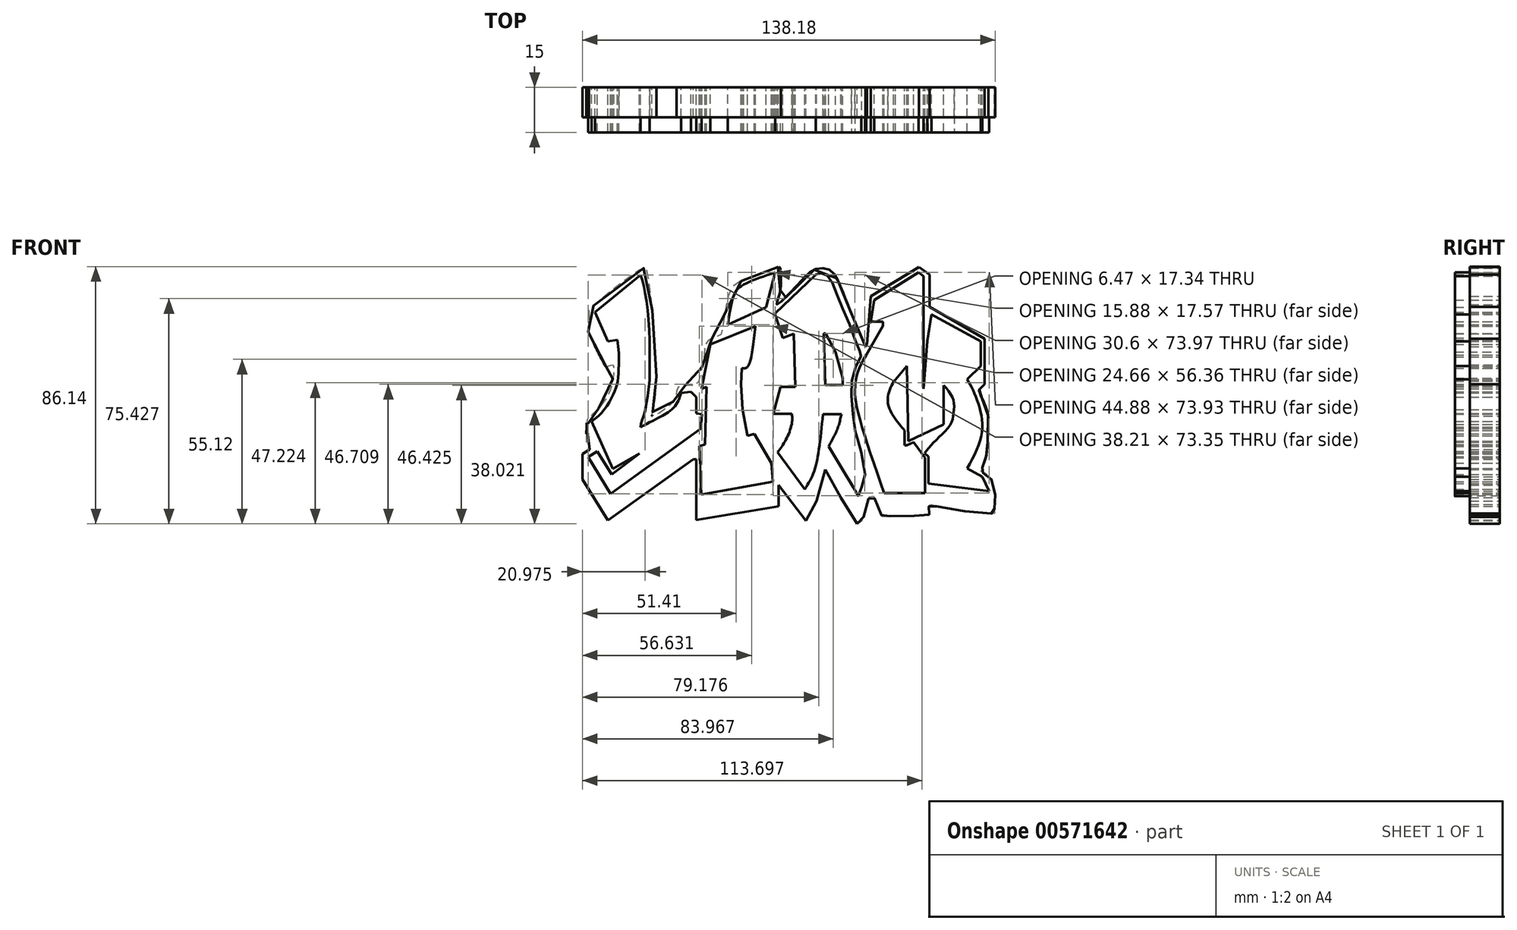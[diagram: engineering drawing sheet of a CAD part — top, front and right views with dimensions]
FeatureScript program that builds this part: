
annotation { "Feature Type Name" : "Feature", "Feature Type Description" : "" }
export const myFeature = defineFeature(function(context is Context, id is Id, definition is map)
    precondition{}
    {
        {
            var Q0;
            Q0=qCreatedBy(makeId("Front.planeOp"),FACE);
            var sketch = newSketch(context, id + "F0", { "sketchPlane" : qUnion([Q0])});
            skLineSegment(sketch, "E0", {"start": v(-63.99, 55.95) * mm, "end": v(-48.71, 68.45) * mm});
            skLineSegment(sketch, "E1", {"start": v(-63.99, 55.95) * mm, "end": v(-59.7, 46.21) * mm});
            skLineSegment(sketch, "E2", {"start": v(-59.7, 46.21) * mm, "end": v(-56.45, 46.65) * mm});
            skFitSpline(sketch, "E3", {"points": [v(-56.45, 46.65) * mm, v(-56.06, 43.07) * mm, v(-56, 38.38) * mm, v(-56.45, 32.7) * mm, v(-57.57, 29.04) * mm, v(-60.63, 23.63) * mm, v(-65.08, 19.34) * mm], "startDerivative": vector(3.26, -24.64) * mm, "endDerivative": vector(-25.33, -21.05) * mm});
            skLineSegment(sketch, "E4", {"start": v(-65.08, 19.34) * mm, "end": v(-58.06, 3.56) * mm});
            skLineSegment(sketch, "E5", {"start": v(-58.06, 3.56) * mm, "end": v(-49.1, 8.6) * mm});
            skLineSegment(sketch, "E6", {"start": v(-49.1, 8.6) * mm, "end": v(-58.36, 1.6) * mm});
            skLineSegment(sketch, "E7", {"start": v(-58.36, 1.6) * mm, "end": v(-63.16, 9.37) * mm});
            skLineSegment(sketch, "E8", {"start": v(-63.16, 9.37) * mm, "end": v(-66.33, 7.42) * mm});
            skLineSegment(sketch, "E9", {"start": v(-66.33, 7.42) * mm, "end": v(-58.72, -4.9) * mm});
            skLineSegment(sketch, "E10", {"start": v(-58.72, -4.9) * mm, "end": v(-28.61, 17) * mm});
            skLineSegment(sketch, "E11", {"start": v(-28.61, 17) * mm, "end": v(-28.12, 21.8) * mm});
            skLineSegment(sketch, "E12", {"start": v(-28.12, 21.8) * mm, "end": v(-30.13, 22) * mm});
            skLineSegment(sketch, "E13", {"start": v(-30.13, 22) * mm, "end": v(-30.13, 27.56) * mm});
            skLineSegment(sketch, "E14", {"start": v(-30.13, 27.56) * mm, "end": v(-31.81, 29.31) * mm});
            skLineSegment(sketch, "E15", {"start": v(-31.81, 29.31) * mm, "end": v(-35.1, 28.96) * mm});
            skFitSpline(sketch, "E16", {"points": [v(-35.1, 28.96) * mm, v(-35.64, 27.42) * mm, v(-36.86, 24.98) * mm, v(-39.26, 22.6) * mm, v(-42.5, 20.74) * mm, v(-48.76, 17.47) * mm], "startDerivative": vector(-3.5, -10.66) * mm, "endDerivative": vector(-23.82, -12.44) * mm});
            skFitSpline(sketch, "E17", {"points": [v(-48.76, 17.47) * mm, v(-48.46, 19.08) * mm, v(-47.3, 22.46) * mm, v(-46.65, 26.08) * mm, v(-45.77, 32) * mm, v(-45.7, 35.08) * mm, v(-45.79, 47.9) * mm, v(-47.16, 62.28) * mm, v(-48.71, 68.45) * mm], "startDerivative": vector(2.53, 21.74) * mm, "endDerivative": vector(-12.5, 41.93) * mm});
            skFitSpline(sketch, "E18", {"points": [v(-19.5, 51.71) * mm, v(-6.66, 57.57) * mm], "startDerivative": vector(12.84, 5.86) * mm, "endDerivative": vector(12.84, 5.86) * mm});
            skFitSpline(sketch, "E19", {"points": [v(-6.66, 57.57) * mm, v(-3.63, 69.28) * mm], "startDerivative": vector(3.03, 11.72) * mm, "endDerivative": vector(3.03, 11.72) * mm});
            skFitSpline(sketch, "E20", {"points": [v(-3.63, 69.28) * mm, v(-14, 65.33) * mm, v(-17.32, 62.09) * mm, v(-19.5, 51.71) * mm], "startDerivative": vector(-31.1, -10.4) * mm, "endDerivative": vector(-4.34, -32.28) * mm});
            skFitSpline(sketch, "E21", {"points": [v(-25.38, 45.16) * mm, v(-10.24, 51.27) * mm], "startDerivative": vector(15.13, 6.11) * mm, "endDerivative": vector(15.13, 6.11) * mm});
            skFitSpline(sketch, "E22", {"points": [v(-10.24, 51.27) * mm, v(-12.86, 37.68) * mm, v(-14.16, 37.15) * mm], "startDerivative": vector(-2.7, -23.89) * mm, "endDerivative": vector(-5.63, -0.3) * mm});
            skFitSpline(sketch, "E23", {"points": [v(-25.38, 45.16) * mm, v(-28.29, 30.32) * mm], "startDerivative": vector(-2.9, -14.84) * mm, "endDerivative": vector(-2.9, -14.84) * mm});
            skFitSpline(sketch, "E24", {"points": [v(-28.29, 30.32) * mm, v(-26.62, 30.97) * mm], "startDerivative": vector(1.66, 0.65) * mm, "endDerivative": vector(1.66, 0.65) * mm});
            skFitSpline(sketch, "E25", {"points": [v(-26.62, 30.97) * mm, v(-27.22, 11.68) * mm], "startDerivative": vector(-0.6, -19.3) * mm, "endDerivative": vector(-0.6, -19.3) * mm});
            skFitSpline(sketch, "E26", {"points": [v(-27.22, 11.68) * mm, v(-29.12, 11.14) * mm], "startDerivative": vector(-1.9, -0.53) * mm, "endDerivative": vector(-1.9, -0.53) * mm});
            skLineSegment(sketch, "E27", {"start": v(-29.12, 11.14) * mm, "end": v(-28.49, -5.09) * mm});
            skLineSegment(sketch, "E28", {"start": v(-28.49, -5.09) * mm, "end": v(-4.46, -0.84) * mm});
            skLineSegment(sketch, "E29", {"start": v(-4.46, -0.84) * mm, "end": v(-4.9, 5.4) * mm});
            skLineSegment(sketch, "E30", {"start": v(-4.9, 5.4) * mm, "end": v(-10.7, 15.23) * mm});
            skLineSegment(sketch, "E31", {"start": v(-10.7, 15.23) * mm, "end": v(-12.9, 14.58) * mm});
            skLineSegment(sketch, "E32", {"start": v(-12.9, 14.58) * mm, "end": v(-14.6, 23.29) * mm});
            skLineSegment(sketch, "E33", {"start": v(-14.6, 23.29) * mm, "end": v(-15.13, 31.9) * mm});
            skLineSegment(sketch, "E34", {"start": v(-15.13, 31.9) * mm, "end": v(-14.9, 37.15) * mm});
            skLineSegment(sketch, "E35", {"start": v(-14.9, 37.15) * mm, "end": v(-14.16, 37.15) * mm});
            skLineSegment(sketch, "E36", {"start": v(-2.91, 9.05) * mm, "end": v(6.26, -3.3) * mm});
            skFitSpline(sketch, "E37", {"points": [v(6.26, -3.3) * mm, v(8.73, 1.14) * mm, v(10.57, 7.5) * mm, v(12.33, 21.75) * mm], "startDerivative": vector(10.14, 16.48) * mm, "endDerivative": vector(3.61, 35.55) * mm});
            skFitSpline(sketch, "E38", {"points": [v(-2.91, 9.05) * mm, v(0, 13.35) * mm, v(1.96, 19.07) * mm, v(1.89, 21.9) * mm], "startDerivative": vector(8.6, 11.07) * mm, "endDerivative": vector(-1.28, 9.71) * mm});
            skFitSpline(sketch, "E39", {"points": [v(1.89, 21.9) * mm, v(-4.33, 21.9) * mm], "startDerivative": vector(-6.21, 0) * mm, "endDerivative": vector(-6.21, 0) * mm});
            skFitSpline(sketch, "E40", {"points": [v(-4.33, 21.9) * mm, v(-1.85, 30.93) * mm], "startDerivative": vector(2.47, 9.03) * mm, "endDerivative": vector(2.47, 9.03) * mm});
            skFitSpline(sketch, "E41", {"points": [v(-1.85, 30.93) * mm, v(3.12, 30.93) * mm], "startDerivative": vector(4.97, 0) * mm, "endDerivative": vector(4.97, 0) * mm});
            skLineSegment(sketch, "E42", {"start": v(3.12, 30.93) * mm, "end": v(2.5, 48.73) * mm});
            skLineSegment(sketch, "E43", {"start": v(2.5, 48.73) * mm, "end": v(-1.1, 47.27) * mm});
            skLineSegment(sketch, "E44", {"start": v(-1.1, 47.27) * mm, "end": v(-3.79, 55.45) * mm});
            skLineSegment(sketch, "E45", {"start": v(-3.79, 55.45) * mm, "end": v(9.91, 68.48) * mm});
            skFitSpline(sketch, "E46", {"points": [v(9.91, 68.48) * mm, v(10.91, 68.88) * mm, v(12.7, 68.93) * mm, v(14.75, 67.08) * mm, v(17.25, 61.24) * mm, v(21.8, 50.32) * mm, v(24.79, 42.68) * mm, v(25.22, 41.9) * mm, v(22.92, 36.66) * mm, v(21.88, 27.23) * mm, v(23.54, 14.44) * mm, v(24.75, 10.56) * mm, v(26.4, 2.38) * mm, v(26.4, 1.28) * mm, v(24.25, -5.6) * mm, v(23.9, -5.25) * mm, v(14.22, 11.02) * mm], "startDerivative": vector(31.9, 15.16) * mm, "endDerivative": vector(-109.87, 180.97) * mm});
            skFitSpline(sketch, "E47", {"points": [v(14.22, 11.02) * mm, v(17.16, 16.81) * mm, v(18.5, 21.85) * mm], "startDerivative": vector(6.3, 11.06) * mm, "endDerivative": vector(2.2, 10.59) * mm});
            skFitSpline(sketch, "E48", {"points": [v(18.5, 21.85) * mm, v(12.33, 21.75) * mm], "startDerivative": vector(-6.18, -0.1) * mm, "endDerivative": vector(-6.18, -0.1) * mm});
            skLineSegment(sketch, "E49", {"start": v(32.81, -4.67) * mm, "end": v(46.5, -4.67) * mm});
            skLineSegment(sketch, "E50", {"start": v(46.5, -4.67) * mm, "end": v(46.5, 7.25) * mm});
            skLineSegment(sketch, "E51", {"start": v(46.5, 7.25) * mm, "end": v(42.63, 12.45) * mm});
            skLineSegment(sketch, "E52", {"start": v(42.63, 12.45) * mm, "end": v(40.38, 11.34) * mm});
            skLineSegment(sketch, "E53", {"start": v(40.38, 11.34) * mm, "end": v(39.69, 11.34) * mm});
            skLineSegment(sketch, "E54", {"start": v(39.69, 11.34) * mm, "end": v(39.69, 16.33) * mm});
            skFitSpline(sketch, "E55", {"points": [v(32.81, -4.67) * mm, v(23.71, 23.9) * mm, v(23.06, 30.37) * mm, v(23.8, 35.37) * mm, v(26.4, 41) * mm], "startDerivative": vector(-27.1, 78.42) * mm, "endDerivative": vector(15.63, 28.91) * mm});
            skFitSpline(sketch, "E56", {"points": [v(39.69, 16.33) * mm, v(37.26, 19.22) * mm, v(34.36, 24.27) * mm, v(34.3, 28.72) * mm, v(36.02, 32.82) * mm], "startDerivative": vector(-10.21, 11.55) * mm, "endDerivative": vector(8.26, 16.36) * mm});
            skLineSegment(sketch, "E57", {"start": v(36.61, 33.4) * mm, "end": v(40.42, 37.94) * mm});
            skLineSegment(sketch, "E58", {"start": v(40.42, 37.94) * mm, "end": v(40.94, 12.76) * mm});
            skLineSegment(sketch, "E59", {"start": v(40.94, 12.76) * mm, "end": v(52.75, 18.33) * mm});
            skLineSegment(sketch, "E60", {"start": v(52.75, 18.33) * mm, "end": v(52.75, 31.45) * mm});
            skLineSegment(sketch, "E61", {"start": v(26.88, 41.6) * mm, "end": v(32.39, 51.34) * mm});
            skLineSegment(sketch, "E62", {"start": v(32.39, 51.34) * mm, "end": v(32.39, 52.8) * mm});
            skLineSegment(sketch, "E63", {"start": v(32.39, 52.8) * mm, "end": v(28.32, 52.8) * mm});
            skLineSegment(sketch, "E64", {"start": v(28.32, 52.8) * mm, "end": v(29.45, 60.01) * mm});
            skLineSegment(sketch, "E65", {"start": v(29.45, 60.01) * mm, "end": v(44.4, 69.26) * mm});
            skLineSegment(sketch, "E66", {"start": v(44.4, 69.26) * mm, "end": v(46, 68.08) * mm});
            skLineSegment(sketch, "E67", {"start": v(46, 68.08) * mm, "end": v(46, 30.27) * mm});
            skLineSegment(sketch, "E68", {"start": v(46, 30.27) * mm, "end": v(47.25, 46.36) * mm});
            skLineSegment(sketch, "E69", {"start": v(47.25, 46.36) * mm, "end": v(48.67, 55.2) * mm});
            skLineSegment(sketch, "E70", {"start": v(48.67, 55.2) * mm, "end": v(65.17, 46.12) * mm});
            skLineSegment(sketch, "E71", {"start": v(65.17, 46.12) * mm, "end": v(65.17, 37.93) * mm});
            skLineSegment(sketch, "E72", {"start": v(65.17, 37.93) * mm, "end": v(60.66, 33.48) * mm});
            skFitSpline(sketch, "E73", {"points": [v(60.66, 33.48) * mm, v(62.79, 29.33) * mm, v(65.08, 22.74) * mm, v(65.38, 14.56) * mm, v(60.66, 3.58) * mm], "startDerivative": vector(10.98, -20.03) * mm, "endDerivative": vector(-19.3, -36.15) * mm});
            skFitSpline(sketch, "E74", {"points": [v(60.66, 3.58) * mm, v(65.68, 0.88) * mm], "startDerivative": vector(5.02, -2.7) * mm, "endDerivative": vector(5.02, -2.7) * mm});
            skFitSpline(sketch, "E75", {"points": [v(65.68, 0.88) * mm, v(67.94, -3.97) * mm], "startDerivative": vector(2.26, -4.85) * mm, "endDerivative": vector(2.26, -4.85) * mm});
            skLineSegment(sketch, "E76", {"start": v(67.94, -3.97) * mm, "end": v(47.63, -1.45) * mm});
            skLineSegment(sketch, "E77", {"start": v(47.63, -1.45) * mm, "end": v(47.63, 7.53) * mm});
            skLineSegment(sketch, "E78", {"start": v(47.63, 7.53) * mm, "end": v(46.37, 8.7) * mm});
            skFitSpline(sketch, "E79", {"points": [v(46.37, 8.7) * mm, v(49.9, 12.81) * mm, v(54.76, 17.93) * mm, v(56.1, 22.3) * mm, v(55.85, 26.91) * mm, v(52.75, 31.45) * mm], "startDerivative": vector(15.72, 20.12) * mm, "endDerivative": vector(-18.9, 21.72) * mm});
            skLineSegment(sketch, "E80", {"start": v(26.4, 41) * mm, "end": v(26.88, 41.6) * mm});
            skLineSegment(sketch, "E81", {"start": v(36.02, 32.82) * mm, "end": v(36.61, 33.4) * mm});
            skLineSegment(sketch, "E82", {"start": v(-65.72, 9.95) * mm, "end": v(-68.2, 8.41) * mm});
            skLineSegment(sketch, "E83", {"start": v(-68.2, 8.41) * mm, "end": v(-68.2, 0) * mm});
            skLineSegment(sketch, "E84", {"start": v(-68.2, 0) * mm, "end": v(-59.67, -13.8) * mm});
            skLineSegment(sketch, "E85", {"start": v(-59.67, -13.8) * mm, "end": v(-31.06, 6.64) * mm});
            skLineSegment(sketch, "E86", {"start": v(-31.06, 6.64) * mm, "end": v(-30.07, 6.64) * mm});
            skLineSegment(sketch, "E87", {"start": v(-30.07, 6.64) * mm, "end": v(-30.07, -13.69) * mm});
            skLineSegment(sketch, "E88", {"start": v(-30.07, -13.69) * mm, "end": v(-2.48, -9.1) * mm});
            skLineSegment(sketch, "E89", {"start": v(-2.48, -9.1) * mm, "end": v(-2.48, -1.9) * mm});
            skLineSegment(sketch, "E90", {"start": v(-2.48, -1.9) * mm, "end": v(6.57, -13.91) * mm});
            skLineSegment(sketch, "E91", {"start": v(6.57, -13.91) * mm, "end": v(10.13, -7.26) * mm});
            skLineSegment(sketch, "E92", {"start": v(10.13, -7.26) * mm, "end": v(13.1, 3.3) * mm});
            skLineSegment(sketch, "E93", {"start": v(13.1, 3.3) * mm, "end": v(18.26, -6.08) * mm});
            skLineSegment(sketch, "E94", {"start": v(18.26, -6.08) * mm, "end": v(23.74, -14.93) * mm});
            skPoint(sketch, "E95.10.internal.snap0", {"position": v(8.35, -10.59) * mm});
            skFitSpline(sketch, "E95", {"points": [v(23.74, -14.93) * mm, v(25.9, -12.8) * mm, v(28.62, -5.03) * mm, v(32, -12.32) * mm, v(33.35, -12.48) * mm, v(47.7, -11.98) * mm, v(47.7, -11.3) * mm, v(47.95, -8.62) * mm, v(48.96, -8.7) * mm, v(69.78, -11.4) * mm, v(69.86, -10.59) * mm, v(69.94, -4.68) * mm, v(67.34, 1.62) * mm, v(65.33, 2.38) * mm, v(65.83, 4.39) * mm, v(67.26, 9.5) * mm, v(67.5, 16.98) * mm, v(67.43, 22.43) * mm, v(64.57, 29.73) * mm, v(64.82, 30.24) * mm, v(66.5, 31.83) * mm], "startDerivative": vector(55.31, 23.52) * mm, "endDerivative": vector(54.2, 52.6) * mm});
            skFitSpline(sketch, "E96", {"points": [v(66.5, 31.83) * mm, v(66.5, 47.13) * mm], "startDerivative": vector(0, 15.3) * mm, "endDerivative": vector(0, 15.3) * mm});
            skFitSpline(sketch, "E97", {"points": [v(66.5, 47.13) * mm, v(47.98, 57.7) * mm], "startDerivative": vector(-18.52, 10.58) * mm, "endDerivative": vector(-18.52, 10.58) * mm});
            skFitSpline(sketch, "E98", {"points": [v(47.98, 57.7) * mm, v(47.98, 68.56) * mm], "startDerivative": vector(0, 10.86) * mm, "endDerivative": vector(0, 10.86) * mm});
            skFitSpline(sketch, "E99", {"points": [v(47.98, 68.56) * mm, v(44.52, 71.12) * mm], "startDerivative": vector(-3.46, 2.55) * mm, "endDerivative": vector(-3.46, 2.55) * mm});
            skFitSpline(sketch, "E100", {"points": [v(44.52, 71.12) * mm, v(28.32, 61.24) * mm], "startDerivative": vector(-16.2, -9.87) * mm, "endDerivative": vector(-16.2, -9.87) * mm});
            skFitSpline(sketch, "E101", {"points": [v(28.32, 61.24) * mm, v(27.07, 45.12) * mm], "startDerivative": vector(-1.25, -16.12) * mm, "endDerivative": vector(-1.25, -16.12) * mm});
            skFitSpline(sketch, "E102", {"points": [v(27.07, 45.12) * mm, v(26.4, 44.05) * mm], "startDerivative": vector(-0.68, -1.07) * mm, "endDerivative": vector(-0.68, -1.07) * mm});
            skFitSpline(sketch, "E103", {"points": [v(26.62, 44.4) * mm, v(20.54, 58.71) * mm, v(19.3, 61.98) * mm, v(17.25, 66.78) * mm, v(14.34, 70.25) * mm, v(9.5, 70.25) * mm, v(4.3, 65.71) * mm, v(-3.08, 58.53) * mm, v(-2.42, 61.24) * mm, v(-1.71, 67.52) * mm, v(-2.24, 71.12) * mm, v(-4.08, 70.54) * mm, v(-15.12, 66.39) * mm, v(-19.28, 61.76) * mm, v(-21.71, 48.64) * mm, v(-22.31, 48.14) * mm, v(-26.55, 46.12) * mm, v(-27.2, 43.55) * mm, v(-29.72, 31.83) * mm, v(-30.73, 31.42) * mm, v(-36.31, 30.75) * mm, v(-36.7, 29.2) * mm, v(-38.03, 25.71) * mm, v(-44.79, 21.22) * mm, v(-44.75, 22.4) * mm, v(-43.78, 27.56) * mm, v(-43.78, 44.4) * mm, v(-46.58, 69.86) * mm, v(-47.83, 70.7) * mm, v(-65.8, 56.99) * mm, v(-66, 56.44) * mm, v(-66.25, 49.55) * mm, v(-65.95, 48.8) * mm, v(-60.2, 37.57) * mm, v(-59.7, 37.72) * mm, v(-58.11, 38.22) * mm, v(-58.3, 32.07) * mm, v(-60.64, 26.54) * mm, v(-65.08, 21.5) * mm, v(-66.51, 20.24) * mm, v(-66.8, 17.22) * mm, v(-66.8, 12.35) * mm, v(-65.72, 9.95) * mm], "startDerivative": vector(-178.63, 414.35) * mm, "endDerivative": vector(79.74, -124.12) * mm});
            skLineSegment(sketch, "E104", {"start": v(-14.16, 37.15) * mm, "end": v(-14.16, 37.15) * mm});
            skLineSegment(sketch, "E105", {"start": v(12.53, 48.86) * mm, "end": v(13.18, 48.86) * mm});
            skLineSegment(sketch, "E106", {"start": v(13.18, 48.86) * mm, "end": v(16.5, 42.6) * mm});
            skLineSegment(sketch, "E107", {"start": v(16.5, 42.6) * mm, "end": v(19, 33.87) * mm});
            skLineSegment(sketch, "E108", {"start": v(19, 33.87) * mm, "end": v(19, 31.52) * mm});
            skLineSegment(sketch, "E109", {"start": v(19, 31.52) * mm, "end": v(13.06, 31.52) * mm});
            skLineSegment(sketch, "E110", {"start": v(13.06, 31.52) * mm, "end": v(12.53, 48.86) * mm});
            skSolve(sketch);
        }
        {
            var Q0;
            Q0=makeQuery(id+"F0.imprint","IMPRINT",FACE,{"disambiguationData":[TD([[makeQuery(id+"F0.imprint","IMPRINT",EDGE,{"derivedFrom":sQuery(id+"F0.wireOp",EDGE,"E0")}),-1.0]])]});
            var Q1;
            Q1=makeQuery(id+"F0.imprint","IMPRINT",FACE,{"disambiguationData":[TD([[makeQuery(id+"F0.imprint","IMPRINT",EDGE,{"derivedFrom":sQuery(id+"F0.wireOp",EDGE,"E21")}),-1.0]])]});
            var Q2;
            Q2=makeQuery(id+"F0.imprint","IMPRINT",FACE,{"disambiguationData":[TD([[makeQuery(id+"F0.imprint","IMPRINT",EDGE,{"derivedFrom":sQuery(id+"F0.wireOp",EDGE,"E18")}),1.0]])]});
            var Q3;
            Q3=makeQuery(id+"F0.imprint","IMPRINT",FACE,{"disambiguationData":[TD([[makeQuery(id+"F0.imprint","IMPRINT",EDGE,{"derivedFrom":sQuery(id+"F0.wireOp",EDGE,"E36")}),1.0]])]});
            var Q4;
            Q4=makeQuery(id+"F0.imprint","IMPRINT",FACE,{"disambiguationData":[TD([[makeQuery(id+"F0.imprint","IMPRINT",EDGE,{"derivedFrom":sQuery(id+"F0.wireOp",EDGE,"E49")}),1.0]])]});
            extrude(context, id + "F1", {"entities" : qUnion([Q0, Q1, Q2, Q3, Q4]), "depth" : 15 * mm, "offsetDistance" : 25 * mm});
        }
        {
            var Q0;
            Q0=makeQuery(id+"F0.imprint","IMPRINT",FACE,{"disambiguationData":[TD([[makeQuery(id+"F0.imprint","IMPRINT",EDGE,{"derivedFrom":sQuery(id+"F0.wireOp",EDGE,"E0")}),1.0]])]});
            extrude(context, id + "F2", {"entities" : qUnion([Q0]), "depth" : 10 * mm, "offsetDistance" : 25 * mm});
        }
    });
